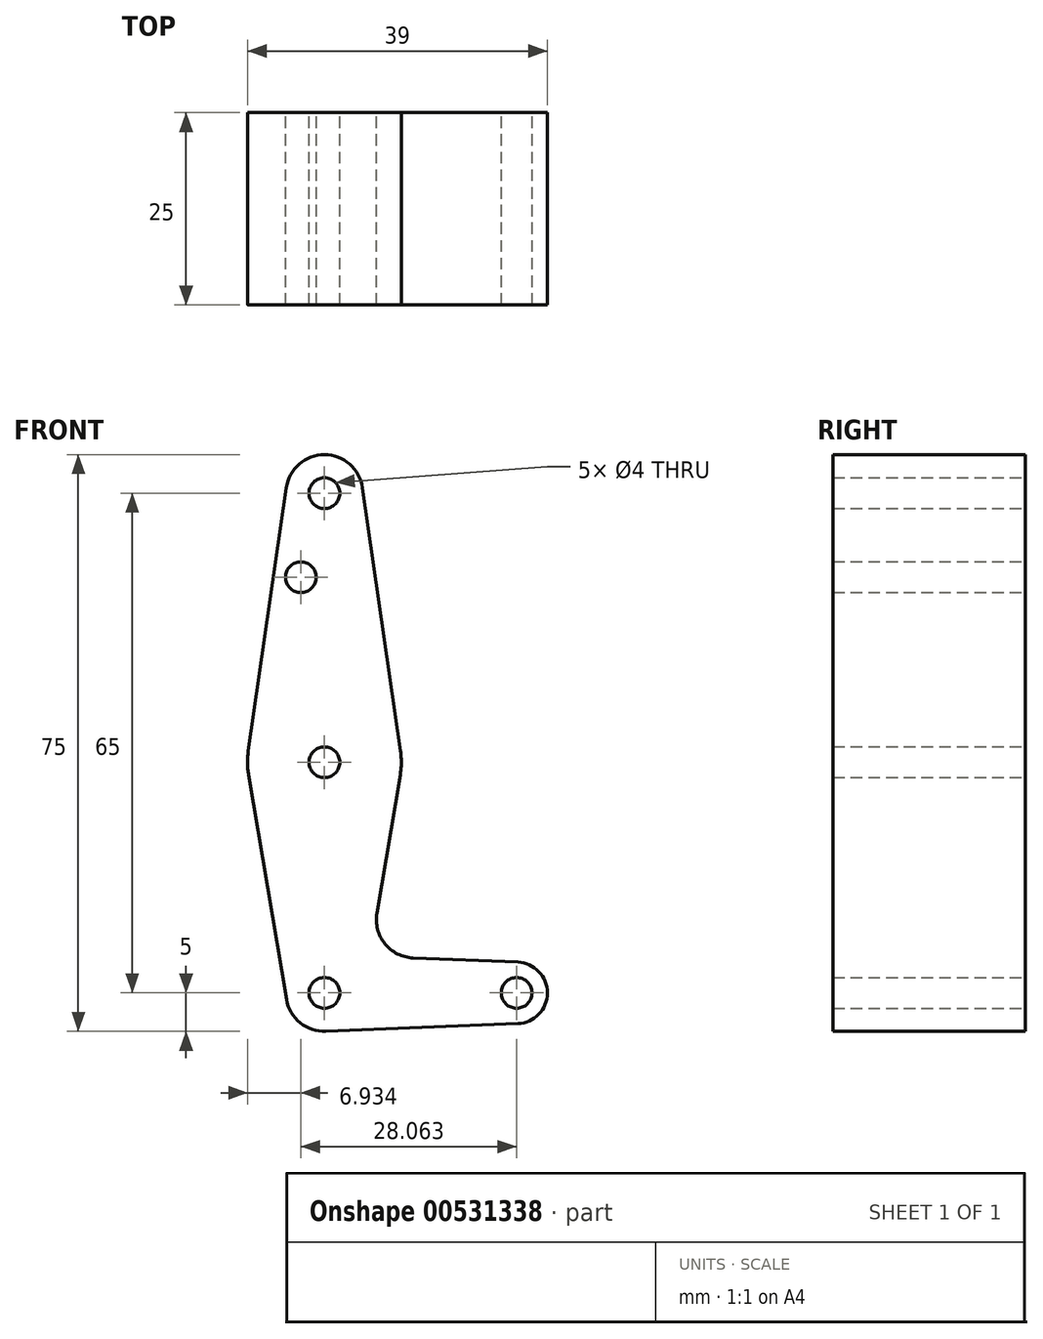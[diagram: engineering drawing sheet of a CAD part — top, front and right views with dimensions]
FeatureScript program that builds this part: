
annotation { "Feature Type Name" : "Feature", "Feature Type Description" : "" }
export const myFeature = defineFeature(function(context is Context, id is Id, definition is map)
    precondition{}
    {
        {
            var Q0;
            Q0=qCreatedBy(makeId("Front.planeOp"),FACE);
            var sketch = newSketch(context, id + "F0", { "sketchPlane" : qUnion([Q0])});
            skCircle(sketch, "E0", {"center": v(-3.47, 0) * mm, "radius": 4 * mm});
            skCircle(sketch, "E1", {"center": v(-28.47, 0) * mm, "radius": 5 * mm});
            skLineSegment(sketch, "E2", {"start": v(-28.47, 0) * mm, "end": v(-3.47, 0) * mm, "construction": true});
            skLineSegment(sketch, "E3", {"start": v(-28.47, 0) * mm, "end": v(-28.47, 30) * mm, "construction": true});
            skLineSegment(sketch, "E4", {"start": v(-28.47, 30) * mm, "end": v(-28.47, 65) * mm, "construction": true});
            skCircle(sketch, "E5", {"center": v(-28.47, 30) * mm, "radius": 10 * mm});
            skCircle(sketch, "E6", {"center": v(-28.47, 65) * mm, "radius": 5 * mm});
            skLineSegment(sketch, "E7", {"start": v(-18.61, 28.33) * mm, "end": v(-21.65, 10.37) * mm});
            skLineSegment(sketch, "E8", {"start": v(-38.33, 28.33) * mm, "end": v(-33.4, -0.83) * mm});
            skLineSegment(sketch, "E9", {"start": v(-23.52, 65.71) * mm, "end": v(-18.58, 31.43) * mm});
            skLineSegment(sketch, "E10", {"start": v(-33.42, 65.71) * mm, "end": v(-38.37, 31.43) * mm});
            skLineSegment(sketch, "E11", {"start": v(-3.31, 4) * mm, "end": v(-16.92, 4.54) * mm});
            skLineSegment(sketch, "E12", {"start": v(-3.31, -4) * mm, "end": v(-28.27, -5) * mm});
            skCircle(sketch, "E13", {"center": v(-28.47, 65) * mm, "radius": 2 * mm});
            skCircle(sketch, "E14", {"center": v(-28.47, 30) * mm, "radius": 2 * mm});
            skCircle(sketch, "E15", {"center": v(-28.47, 0) * mm, "radius": 2 * mm});
            skCircle(sketch, "E16", {"center": v(-3.47, 0) * mm, "radius": 2 * mm});
            skCircle(sketch, "E17", {"center": v(-31.54, 54.07) * mm, "radius": 2 * mm});
            skArc(sketch, "E18.filletArc", {"start": v(-21.65, 10.37) * mm, "mid": v(-20.6, 6.39) * mm, "end": v(-16.92, 4.54) * mm});
            skSolve(sketch);
        }
        {
            var Q0;
            {var subQ0=sQuery(id+"F0.wireOp",EDGE,"E7");Q0=makeQuery(id+"F0.imprint","IMPRINT",FACE,{"disambiguationData":[TD([[makeQuery(id+"F0.imprint","IMPRINT",EDGE,{"derivedFrom":subQ0}),-1.0]])]});}
            var Q1;
            Q1=makeQuery(id+"F0.imprint","IMPRINT",FACE,{"disambiguationData":[TD([[makeQuery(id+"F0.imprint","IMPRINT",EDGE,{"derivedFrom":sQuery(id+"F0.wireOp",EDGE,"E15")}),-1.0]])]});
            var Q2;
            Q2=makeQuery(id+"F0.imprint","IMPRINT",FACE,{"disambiguationData":[TD([[makeQuery(id+"F0.imprint","IMPRINT",EDGE,{"derivedFrom":sQuery(id+"F0.wireOp",EDGE,"E16")}),-1.0]])]});
            var Q3;
            Q3=makeQuery(id+"F0.imprint","IMPRINT",FACE,{"disambiguationData":[TD([[makeQuery(id+"F0.imprint","IMPRINT",EDGE,{"derivedFrom":sQuery(id+"F0.wireOp",EDGE,"E14")}),-1.0]])]});
            var Q4;
            {var subQ1=sQuery(id+"F0.wireOp",EDGE,"E9");Q4=makeQuery(id+"F0.imprint","IMPRINT",FACE,{"disambiguationData":[TD([[makeQuery(id+"F0.imprint","IMPRINT",EDGE,{"derivedFrom":subQ1}),-1.0]])]});}
            var Q5;
            Q5=makeQuery(id+"F0.imprint","IMPRINT",FACE,{"disambiguationData":[TD([[makeQuery(id+"F0.imprint","IMPRINT",EDGE,{"derivedFrom":sQuery(id+"F0.wireOp",EDGE,"E13")}),-1.0]])]});
            extrude(context, id + "F1", {"entities" : qUnion([Q0, Q1, Q2, Q3, Q4, Q5]), "depth" : 25 * mm, "offsetDistance" : 25 * mm});
        }
    });
